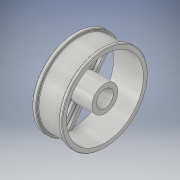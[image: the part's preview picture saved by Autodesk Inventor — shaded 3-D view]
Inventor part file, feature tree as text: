
AUTODESK INVENTOR PART (.ipt)
format: ipt  version: 2018 (Build 220112000, 112)  size: 408,064 bytes
history: native  units: in
note: dims shown in document units (in); Inventor stores cm internally (conversion verified against a paired STEP export)
features: sketch x8, extrude x6, projected_geometry x4, revolve x2, pattern_circular x2, fillet x2
ambient origin geometry x8: Origin, YZ Plane, XZ Plane, XY Plane, X Axis, Y Axis, Z Axis, Center Point
bodies: Solid1 (feature_tree)
feature tree (24):
  revolve  "Revolution1"  [1 undecoded]
  revolve  "Revolution2"  [1 undecoded]
  extrude  "Extrusion1"  Depth=0.11in
  pattern_circular  "Circular Pattern1"  [2 undecoded]
  extrude  "Extrusion2"  Depth=0.1in
  pattern_circular  "Circular Pattern2"  [2 undecoded]
  extrude  "Extrusion3"  Depth=0.05in
  extrude  "Extrusion4"  TaperAngle=90.0deg  [1 undecoded]
  extrude  "Extrusion5"  Depth=0.01in
  fillet  "Fillet1"  Radius=0.04in
  extrude  "Extrusion6"  Depth=0.01in TaperAngle=0.0deg
  fillet  "Fillet2"  Radius=1.9685in
  sketch  "Sketch1"  dims[d0=0.695in d1=0.15in]
  sketch  "Sketch2"  dims[d2=0.07in d3=0.11in]
  projected_geometry  "Projected Loop1"
  projected_geometry  "Projected Loop2"
  projected_geometry  "Projected Loop3"
  projected_geometry  "Projected Loop4"
  sketch  "Sketch3"  dims[d4=0.42in d5=0.11in]
  sketch  "Sketch4"  dims[d6=0.07in]
  sketch  "Sketch5"  dims[d7=0.15in]
  sketch  "Sketch6"  dims[d8=0.01in]
  sketch  "Sketch7"  dims[d9=90.0deg]
  sketch  "Sketch8"  dims[d10=0.1in d11=0.5425in d12=0.1in d13=0.46in d14=0.05in d15=90.0deg d16=0.04in d17=0.04in d18=1.0in d19=0.0in d20=1.9685in d21=360.0deg d23=0.07in d24=0.07in d25=0.07in d26=0.07in d27=1.0in d28=0.0in d29=1.9685in d30=360.0deg d32=0.02in d33=0.0in d34=0.02in d35=0.0in d36=2.0in d37=0.0in d38=0.01in d39=1.55in d40=20.0in d41=0.0in d42=0.01in]
note: 7 required parameter values undecoded (feature->parameter linkage not recoverable at this tier; creation-order binding heuristic only, values carry confidence <= 0.55)